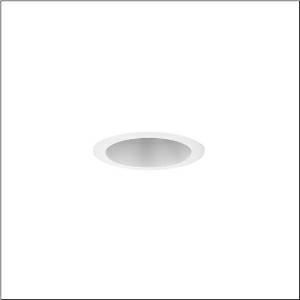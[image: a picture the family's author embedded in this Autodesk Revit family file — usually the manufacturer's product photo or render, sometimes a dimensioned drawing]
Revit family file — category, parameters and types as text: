
# Revit family: lunis_31_mini_51dn167e31
name_source: partatom
category: Lighting Fixtures
units: mm (PartAtom-declared; Revit-internal decimal feet)

## family parameters
Cut with Voids When Loaded = No
Host = Face
Light Source = No
Part Type = Normal
Room Calculation Point = No
Round Connector Dimension = Use Diameter
Shared = No

## types (1)
- Lunis 31 mini (1 x LED, 1000 lm, 8.3 W, 3000K)
    Apparent Load = 8 VA
    CIE Flux Codes = 69 93 99 100 100
    Color Rendering = 80
    Color Temperature = 3000K
    Default Elevation = 1800 mm
    Description = Lunis 31,  mini, downlight, light control with reflector, light emission: direct distribution, LED rated luminous flux: 1.000lm, light colour: 830, control gear: ECG, mains connection: 220..240V, AC, 50/60Hz, housing, white, protection rating (complete): IP20, insulation class (complete): insulation class II (safety insulation), certification: CE, packaging unit: 1 piece
    Height = 0 mm  [stored 0 ft]
    Lamp = 1 x LED
    Lamp Light Flux = 1000 lm
    Lamp Power = 8.3 W
    Lamp count = 1
    Length = 188 mm  [stored 0.616798 ft]
    Luminous efficacy = 120 lm/W
    Manufacturer = Siteco
    ModVariant = No
    Model = 51DN167E31
    Mounting Place = Ceiling
    Mounting Type = Recessed
    Number of Poles = 1
    OnlyDefault = Yes
    Power Factor = 1
    Product Name = Lunis 31 mini
    Product group = downlight | ceiling recessed
    ProductGroupID = 402
    Protection Class = Protection class II
    Protection Degree = IP 20
    RLX_Detail_Level = 1
    RlxData = <blob elided: 21729 chars, md5=e6682277>
    Socket = socket
    Standby Power = 0 W
    System Light Flux = 1000 lm
    System Power = 8 W
    Type Comments = Product without accessories
    Type Image = l_1005624.jpg
    URL = http://relux.com
    VarID = ---
    Voltage = 0 V
    Weight = 0.00 kg
    Width = 0 mm  [stored 0 ft]

note: [stored X ft] marks values corroborated as IEEE doubles in the binary element streams (Revit-internal decimal feet)

## geometry (parser evidence)
native form markers: Blend x4, Sweep x11
no freeform markers — native parametric forms only
